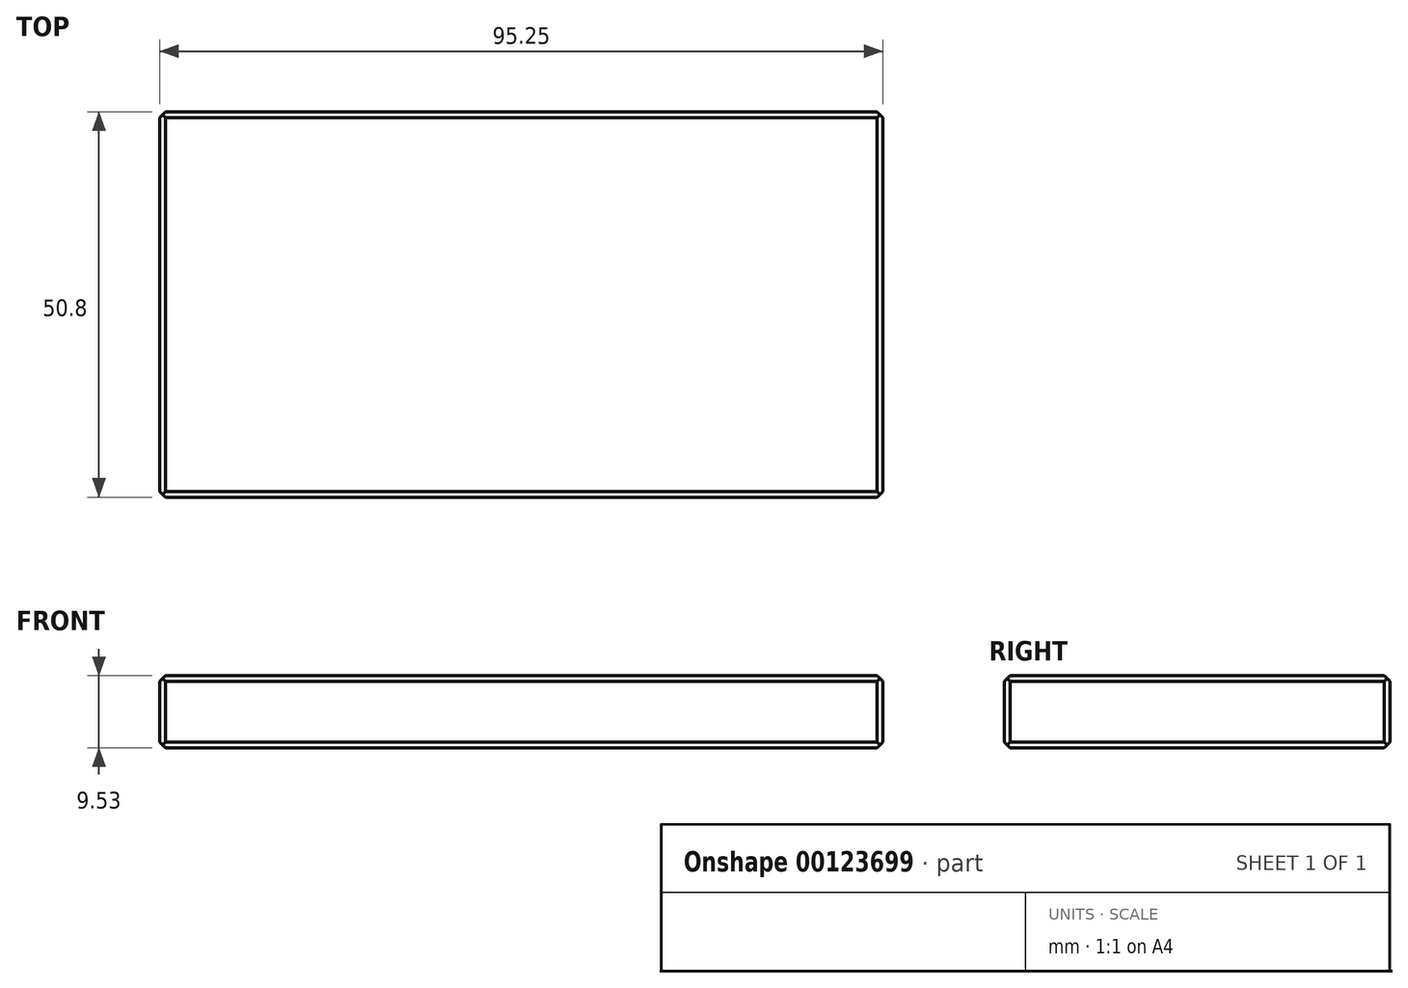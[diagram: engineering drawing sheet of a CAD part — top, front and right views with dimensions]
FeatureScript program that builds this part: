
annotation { "Feature Type Name" : "Feature", "Feature Type Description" : "" }
export const myFeature = defineFeature(function(context is Context, id is Id, definition is map)
    precondition{}
    {
        {
            var Q0;
            Q0=qCreatedBy(makeId("Top.planeOp"),FACE);
            var sketch = newSketch(context, id + "F0", { "sketchPlane" : qUnion([Q0])});
            skLineSegment(sketch, "E0.bottom", {"start": v(-35.1, -27.7) * mm, "end": v(60.16, -27.7) * mm});
            skLineSegment(sketch, "E0.top", {"start": v(-35.1, 23.1) * mm, "end": v(60.16, 23.1) * mm});
            skLineSegment(sketch, "E0.left", {"start": v(-35.1, -27.7) * mm, "end": v(-35.1, 23.1) * mm});
            skLineSegment(sketch, "E0.right", {"start": v(60.16, -27.7) * mm, "end": v(60.16, 23.1) * mm});
            skSolve(sketch);
        }
        {
            var Q0;
            Q0=makeQuery(id+"F0.imprint","IMPRINT",FACE,{"disambiguationData":[TD([[makeQuery(id+"F0.imprint","IMPRINT",EDGE,{"derivedFrom":sQuery(id+"F0.wireOp",EDGE,"E0.bottom")}),1.0]])]});
            extrude(context, id + "F1", {"entities" : qUnion([Q0]), "depth" : 9.52 * mm});
        }
        {
            var Q0;
            Q0=makeQuery(id+"F1.opExtrude","CAP_FACE",FACE,{"disambiguationData":[OSD([sQuery(id+"F0.wireOp",EDGE,"E0.bottom"),sQuery(id+"F0.wireOp",EDGE,"E0.top"),sQuery(id+"F0.wireOp",EDGE,"E0.left"),sQuery(id+"F0.wireOp",EDGE,"E0.right")])],"isStart":false});
            var Q1;
            Q1=makeQuery(id+"F1.opExtrude","CAP_FACE",FACE,{"disambiguationData":[OSD([sQuery(id+"F0.wireOp",EDGE,"E0.bottom"),sQuery(id+"F0.wireOp",EDGE,"E0.top"),sQuery(id+"F0.wireOp",EDGE,"E0.left"),sQuery(id+"F0.wireOp",EDGE,"E0.right")])],"isStart":true});
            chamfer(context, id + "F2", {"entities" : qUnion([Q0, Q1]), "width" : 0.76 * mm, "tangentPropagation" : true});
        }
        {
            var Q0;
            Q0=makeQuery(id+"F1.opExtrude","SWEPT_EDGE",EDGE,{"disambiguationData":[OSD([sQuery(id+"F0.wireOp",EDGE,"E0.bottom"),sQuery(id+"F0.wireOp",EDGE,"E0.right")])]});
            var Q1;
            Q1=makeQuery(id+"F1.opExtrude","SWEPT_EDGE",EDGE,{"disambiguationData":[OSD([sQuery(id+"F0.wireOp",EDGE,"E0.bottom"),sQuery(id+"F0.wireOp",EDGE,"E0.left")])]});
            var Q2;
            Q2=makeQuery(id+"F1.opExtrude","SWEPT_EDGE",EDGE,{"disambiguationData":[OSD([sQuery(id+"F0.wireOp",EDGE,"E0.top"),sQuery(id+"F0.wireOp",EDGE,"E0.right")])]});
            var Q3;
            Q3=makeQuery(id+"F1.opExtrude","SWEPT_EDGE",EDGE,{"disambiguationData":[OSD([sQuery(id+"F0.wireOp",EDGE,"E0.top"),sQuery(id+"F0.wireOp",EDGE,"E0.left")])]});
            chamfer(context, id + "F3", {"entities" : qUnion([Q0, Q1, Q2, Q3]), "width" : 0.76 * mm, "tangentPropagation" : true});
        }
    });
